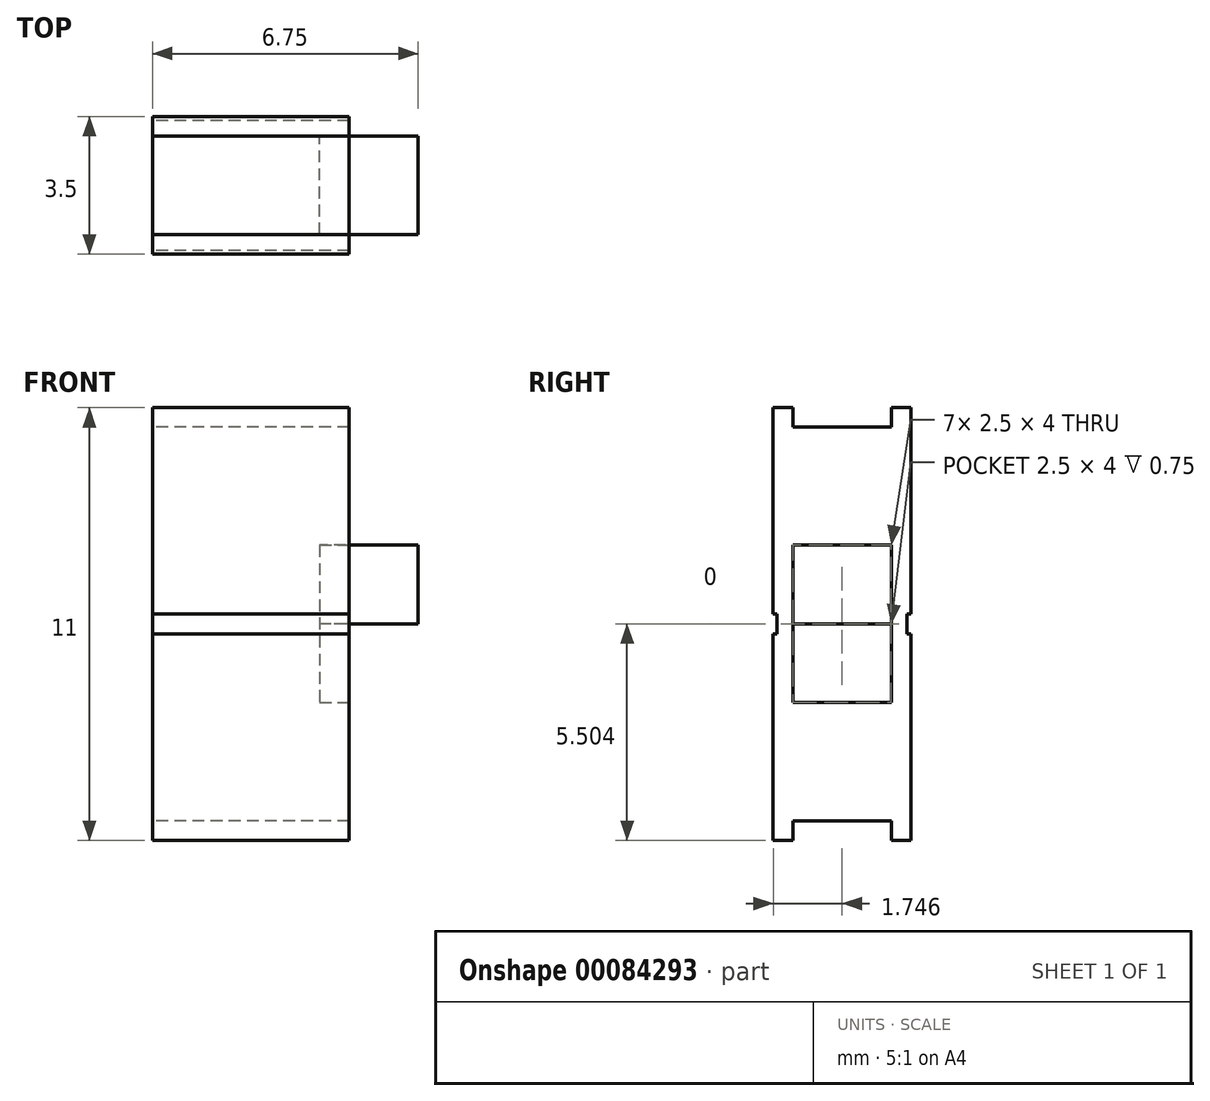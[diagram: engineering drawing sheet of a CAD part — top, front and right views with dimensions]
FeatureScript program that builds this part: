
annotation { "Feature Type Name" : "Feature", "Feature Type Description" : "" }
export const myFeature = defineFeature(function(context is Context, id is Id, definition is map)
    precondition{}
    {
        {
            var Q0;
            Q0=qCreatedBy(makeId("Right.planeOp"),FACE);
            var sketch = newSketch(context, id + "F0", { "sketchPlane" : qUnion([Q0])});
            skLineSegment(sketch, "E0.bottom", {"start": v(-11.53, 0.38) * mm, "end": v(-8.03, 0.38) * mm});
            skLineSegment(sketch, "E0.top", {"start": v(-11.53, -10.62) * mm, "end": v(-8.03, -10.62) * mm});
            skLineSegment(sketch, "E0.left", {"start": v(-11.53, 0.38) * mm, "end": v(-11.53, -10.62) * mm});
            skLineSegment(sketch, "E0.right", {"start": v(-8.03, 0.38) * mm, "end": v(-8.03, -10.62) * mm});
            skLineSegment(sketch, "E1.bottom", {"start": v(-11.03, 0.38) * mm, "end": v(-8.53, 0.38) * mm});
            skLineSegment(sketch, "E1.top", {"start": v(-11.03, -0.12) * mm, "end": v(-8.53, -0.12) * mm});
            skLineSegment(sketch, "E1.left", {"start": v(-11.03, 0.38) * mm, "end": v(-11.03, -0.12) * mm});
            skLineSegment(sketch, "E1.right", {"start": v(-8.53, 0.38) * mm, "end": v(-8.53, -0.12) * mm});
            skLineSegment(sketch, "E2.bottom", {"start": v(-8.53, -10.62) * mm, "end": v(-11.03, -10.62) * mm});
            skLineSegment(sketch, "E2.top", {"start": v(-8.53, -10.12) * mm, "end": v(-11.03, -10.12) * mm});
            skLineSegment(sketch, "E2.left", {"start": v(-8.53, -10.62) * mm, "end": v(-8.53, -10.12) * mm});
            skLineSegment(sketch, "E2.right", {"start": v(-11.03, -10.62) * mm, "end": v(-11.03, -10.12) * mm});
            skLineSegment(sketch, "E3.bottom", {"start": v(-8.13, -5.37) * mm, "end": v(-7.93, -5.37) * mm});
            skLineSegment(sketch, "E3.top", {"start": v(-8.13, -4.87) * mm, "end": v(-7.93, -4.87) * mm});
            skLineSegment(sketch, "E3.left", {"start": v(-8.13, -5.37) * mm, "end": v(-8.13, -4.87) * mm});
            skLineSegment(sketch, "E3.right", {"start": v(-7.93, -5.37) * mm, "end": v(-7.93, -4.87) * mm});
            skPoint(sketch, "E3.middle", {"position": v(-8.03, -5.12) * mm});
            skLineSegment(sketch, "E4.bottom", {"start": v(-11.43, -4.87) * mm, "end": v(-12.1, -4.87) * mm});
            skLineSegment(sketch, "E4.top", {"start": v(-11.43, -5.37) * mm, "end": v(-12.1, -5.37) * mm});
            skLineSegment(sketch, "E4.left", {"start": v(-11.43, -4.87) * mm, "end": v(-11.43, -5.37) * mm});
            skLineSegment(sketch, "E4.right", {"start": v(-12.1, -4.87) * mm, "end": v(-12.1, -5.37) * mm});
            skSolve(sketch);
        }
        {
            var Q0;
            {var subQ0=sQuery(id+"F0.wireOp",EDGE,"E0.left");Q0=makeQuery(id+"F0.imprint","IMPRINT",FACE,{"disambiguationData":[TD([[makeQuery(id+"F0.imprint","IMPRINT",EDGE,{"derivedFrom":subQ0}),1.0]])]});}
            extrude(context, id + "F1", {"entities" : qUnion([Q0]), "depth" : 5 * mm});
        }
        {
            var Q0;
            Q0=makeQuery(id+"F1.opExtrude","CAP_FACE",FACE,{"disambiguationData":[OSD([sQuery(id+"F0.wireOp",EDGE,"E0.bottom"),sQuery(id+"F0.wireOp",EDGE,"E0.top"),sQuery(id+"F0.wireOp",EDGE,"E0.left"),sQuery(id+"F0.wireOp",EDGE,"E0.right"),sQuery(id+"F0.wireOp",EDGE,"E1.top"),sQuery(id+"F0.wireOp",EDGE,"E1.left"),sQuery(id+"F0.wireOp",EDGE,"E1.right"),sQuery(id+"F0.wireOp",EDGE,"E2.top"),sQuery(id+"F0.wireOp",EDGE,"E2.left"),sQuery(id+"F0.wireOp",EDGE,"E2.right"),sQuery(id+"F0.wireOp",EDGE,"E3.bottom"),sQuery(id+"F0.wireOp",EDGE,"E3.top"),sQuery(id+"F0.wireOp",EDGE,"E3.left"),sQuery(id+"F0.wireOp",EDGE,"E4.bottom"),sQuery(id+"F0.wireOp",EDGE,"E4.top"),sQuery(id+"F0.wireOp",EDGE,"E4.left")])],"isStart":false});
            var sketch = newSketch(context, id + "F2", { "sketchPlane" : qUnion([Q0])});
            skLineSegment(sketch, "E5.bottom", {"start": v(-11.03, -3.12) * mm, "end": v(-8.53, -3.12) * mm});
            skLineSegment(sketch, "E5.top", {"start": v(-11.03, -7.12) * mm, "end": v(-8.53, -7.12) * mm});
            skLineSegment(sketch, "E5.left", {"start": v(-11.03, -3.12) * mm, "end": v(-11.03, -7.12) * mm});
            skLineSegment(sketch, "E5.right", {"start": v(-8.53, -3.12) * mm, "end": v(-8.53, -7.12) * mm});
            skSolve(sketch);
        }
        {
            var Q0;
            Q0=makeQuery(id+"F2.imprint","IMPRINT",FACE,{"disambiguationData":[TD([[makeQuery(id+"F2.imprint","IMPRINT",EDGE,{"derivedFrom":sQuery(id+"F2.wireOp",EDGE,"E5.bottom")}),-1.0]])]});
            extrude(context, id + "F3", {"entities" : qUnion([Q0]), "operationType" : NewBodyOperationType.REMOVE, "oppositeDirection" : true, "depth" : 0.75 * mm});
        }
        {
            var Q0;
            Q0=makeQuery(id+"F3.boolean.opBoolean","COPY",FACE,{"derivedFrom":makeQuery(id+"F3.opExtrude","CAP_FACE",FACE,{"disambiguationData":[OSD([sQuery(id+"F2.wireOp",EDGE,"E5.bottom"),sQuery(id+"F2.wireOp",EDGE,"E5.top"),sQuery(id+"F2.wireOp",EDGE,"E5.left"),sQuery(id+"F2.wireOp",EDGE,"E5.right")])],"isStart":false})});
            var sketch = newSketch(context, id + "F4", { "sketchPlane" : qUnion([Q0])});
            skLineSegment(sketch, "E6.bottom", {"start": v(-11.03, -3.12) * mm, "end": v(-8.53, -3.12) * mm});
            skLineSegment(sketch, "E6.top", {"start": v(-11.03, -5.12) * mm, "end": v(-8.53, -5.12) * mm});
            skLineSegment(sketch, "E6.left", {"start": v(-11.03, -3.12) * mm, "end": v(-11.03, -5.12) * mm});
            skLineSegment(sketch, "E6.right", {"start": v(-8.53, -3.12) * mm, "end": v(-8.53, -5.12) * mm});
            skSolve(sketch);
        }
        {
            var Q0;
            Q0=makeQuery(id+"F4.imprint","IMPRINT",FACE,{"disambiguationData":[TD([[makeQuery(id+"F4.imprint","IMPRINT",EDGE,{"derivedFrom":sQuery(id+"F4.wireOp",EDGE,"E6.bottom")}),-1.0]])]});
            extrude(context, id + "F5", {"entities" : qUnion([Q0]), "depth" : 2.5 * mm});
        }
    });
